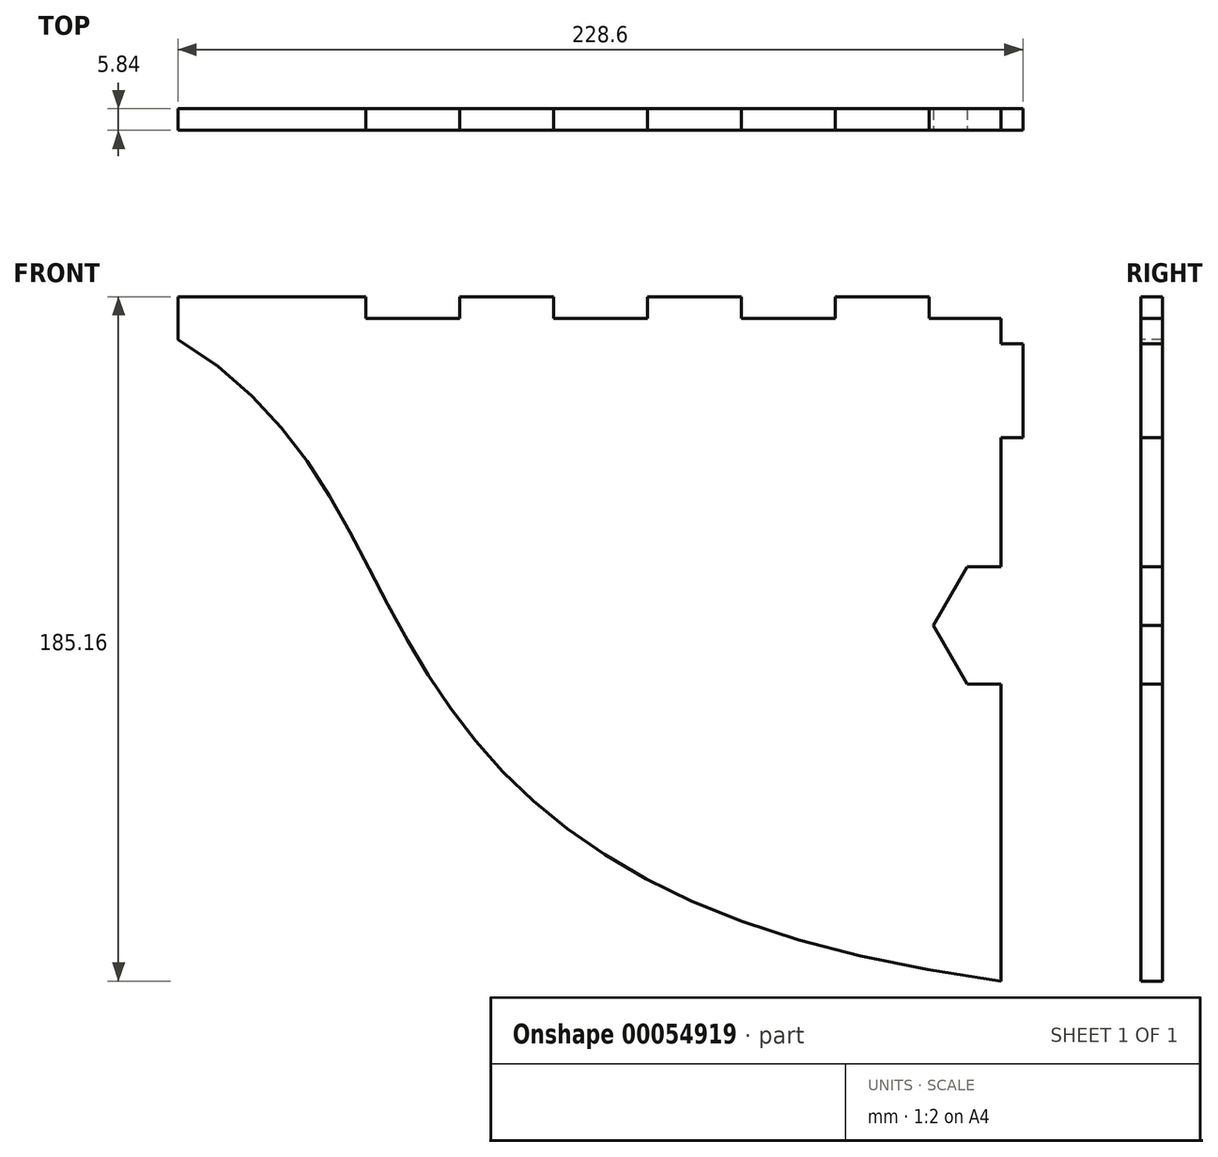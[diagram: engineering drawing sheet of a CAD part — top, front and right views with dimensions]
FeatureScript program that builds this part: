
annotation { "Feature Type Name" : "Feature", "Feature Type Description" : "" }
export const myFeature = defineFeature(function(context is Context, id is Id, definition is map)
    precondition{}
    {
        {
            var Q0;
            Q0=qCreatedBy(makeId("Front.planeOp"),FACE);
            var sketch = newSketch(context, id + "F0", { "sketchPlane" : qUnion([Q0])});
            skLineSegment(sketch, "E0.bottom", {"start": v(-113.95, 205.98) * mm, "end": v(165.45, 205.98) * mm});
            skLineSegment(sketch, "E0.top", {"start": v(-113.95, -124.22) * mm, "end": v(165.45, -124.22) * mm});
            skLineSegment(sketch, "E0.left", {"start": v(-113.95, 205.98) * mm, "end": v(-113.95, -124.22) * mm});
            skLineSegment(sketch, "E0.right", {"start": v(165.45, 205.98) * mm, "end": v(165.45, -124.22) * mm});
            skSolve(sketch);
        }
        {
            var Q0;
            Q0=makeQuery(id+"F0.imprint","IMPRINT",FACE,{"disambiguationData":[TD([[makeQuery(id+"F0.imprint","IMPRINT",EDGE,{"derivedFrom":sQuery(id+"F0.wireOp",EDGE,"E0.bottom")}),-1.0]])]});
            extrude(context, id + "F1", {"entities" : qUnion([Q0]), "depth" : 5.84 * mm});
        }
        {
            var Q0;
            Q0=makeQuery(id+"F1.opExtrude","CAP_FACE",FACE,{"disambiguationData":[OSD([sQuery(id+"F0.wireOp",EDGE,"E0.bottom"),sQuery(id+"F0.wireOp",EDGE,"E0.top"),sQuery(id+"F0.wireOp",EDGE,"E0.left"),sQuery(id+"F0.wireOp",EDGE,"E0.right")])],"isStart":false});
            var sketch = newSketch(context, id + "F2", { "sketchPlane" : qUnion([Q0])});
            skLineSegment(sketch, "E1", {"start": v(165.45, -118.38) * mm, "end": v(140.05, -118.38) * mm});
            skLineSegment(sketch, "E2", {"start": v(140.05, -118.38) * mm, "end": v(140.05, -124.22) * mm});
            skLineSegment(sketch, "E3", {"start": v(140.05, -124.22) * mm, "end": v(114.65, -124.22) * mm});
            skLineSegment(sketch, "E4", {"start": v(114.65, -124.22) * mm, "end": v(114.65, -118.38) * mm});
            skLineSegment(sketch, "E5", {"start": v(114.65, -118.38) * mm, "end": v(89.25, -118.38) * mm});
            skLineSegment(sketch, "E6", {"start": v(89.25, -118.38) * mm, "end": v(89.25, -124.22) * mm});
            skLineSegment(sketch, "E7", {"start": v(89.25, -124.22) * mm, "end": v(63.85, -124.22) * mm});
            skLineSegment(sketch, "E8", {"start": v(63.85, -124.22) * mm, "end": v(63.85, -118.38) * mm});
            skLineSegment(sketch, "E9", {"start": v(63.85, -118.38) * mm, "end": v(38.45, -118.38) * mm});
            skLineSegment(sketch, "E10", {"start": v(38.45, -118.38) * mm, "end": v(38.45, -124.22) * mm});
            skLineSegment(sketch, "E11", {"start": v(38.45, -124.22) * mm, "end": v(13.05, -124.22) * mm});
            skLineSegment(sketch, "E12", {"start": v(13.05, -124.22) * mm, "end": v(13.05, -118.38) * mm});
            skLineSegment(sketch, "E13", {"start": v(13.05, -118.38) * mm, "end": v(-12.35, -118.38) * mm});
            skLineSegment(sketch, "E14", {"start": v(-12.35, -118.38) * mm, "end": v(-12.35, -124.22) * mm});
            skLineSegment(sketch, "E15", {"start": v(-12.35, -124.22) * mm, "end": v(-37.75, -124.22) * mm});
            skLineSegment(sketch, "E16", {"start": v(-37.75, -124.22) * mm, "end": v(-37.75, -118.38) * mm});
            skLineSegment(sketch, "E17", {"start": v(-37.75, -118.38) * mm, "end": v(-113.95, -118.38) * mm});
            skLineSegment(sketch, "E18", {"start": v(-113.95, -118.38) * mm, "end": v(-113.95, -124.22) * mm});
            skLineSegment(sketch, "E19", {"start": v(-113.95, -124.22) * mm, "end": v(-37.75, -124.22) * mm});
            skLineSegment(sketch, "E20.bottom", {"start": v(165.45, -98.82) * mm, "end": v(159.6, -98.82) * mm});
            skLineSegment(sketch, "E20.top", {"start": v(165.45, -73.42) * mm, "end": v(159.6, -73.42) * mm});
            skLineSegment(sketch, "E20.left", {"start": v(165.45, -98.82) * mm, "end": v(165.45, -73.42) * mm});
            skLineSegment(sketch, "E20.right", {"start": v(159.6, -98.82) * mm, "end": v(159.6, -73.42) * mm});
            skLineSegment(sketch, "E21.bottom", {"start": v(165.45, -48.02) * mm, "end": v(159.6, -48.02) * mm});
            skLineSegment(sketch, "E21.top", {"start": v(165.45, -9.92) * mm, "end": v(159.6, -9.92) * mm});
            skLineSegment(sketch, "E21.left", {"start": v(165.45, -48.02) * mm, "end": v(165.45, -9.92) * mm});
            skLineSegment(sketch, "E21.right", {"start": v(159.6, -48.02) * mm, "end": v(159.6, -9.92) * mm});
            skLineSegment(sketch, "E22.bottom", {"start": v(-113.95, -98.82) * mm, "end": v(-108.1, -98.82) * mm});
            skLineSegment(sketch, "E22.top", {"start": v(-113.95, -73.42) * mm, "end": v(-108.1, -73.42) * mm});
            skLineSegment(sketch, "E22.left", {"start": v(-113.95, -98.82) * mm, "end": v(-113.95, -73.42) * mm});
            skLineSegment(sketch, "E22.right", {"start": v(-108.1, -98.82) * mm, "end": v(-108.1, -73.42) * mm});
            skLineSegment(sketch, "E23.bottom", {"start": v(-113.95, -48.02) * mm, "end": v(-108.1, -48.02) * mm});
            skLineSegment(sketch, "E23.top", {"start": v(-113.95, -22.62) * mm, "end": v(-108.1, -22.62) * mm});
            skLineSegment(sketch, "E23.left", {"start": v(-113.95, -48.02) * mm, "end": v(-113.95, -22.62) * mm});
            skLineSegment(sketch, "E23.right", {"start": v(-108.1, -48.02) * mm, "end": v(-108.1, -22.62) * mm});
            skLineSegment(sketch, "E24.bottom", {"start": v(-113.95, 2.78) * mm, "end": v(-108.1, 2.78) * mm});
            skLineSegment(sketch, "E24.top", {"start": v(-113.95, 28.18) * mm, "end": v(-108.1, 28.18) * mm});
            skLineSegment(sketch, "E24.left", {"start": v(-113.95, 2.78) * mm, "end": v(-113.95, 28.18) * mm});
            skLineSegment(sketch, "E24.right", {"start": v(-108.1, 2.78) * mm, "end": v(-108.1, 28.18) * mm});
            skLineSegment(sketch, "E25.bottom", {"start": v(-113.95, 104.38) * mm, "end": v(-108.1, 104.38) * mm});
            skLineSegment(sketch, "E25.top", {"start": v(-113.95, 129.78) * mm, "end": v(-108.1, 129.78) * mm});
            skLineSegment(sketch, "E25.left", {"start": v(-113.95, 104.38) * mm, "end": v(-113.95, 129.78) * mm});
            skLineSegment(sketch, "E25.right", {"start": v(-108.1, 104.38) * mm, "end": v(-108.1, 129.78) * mm});
            skLineSegment(sketch, "E26.bottom", {"start": v(-113.95, 53.58) * mm, "end": v(-108.1, 53.58) * mm});
            skLineSegment(sketch, "E26.top", {"start": v(-113.95, 78.98) * mm, "end": v(-108.1, 78.98) * mm});
            skLineSegment(sketch, "E26.left", {"start": v(-113.95, 53.58) * mm, "end": v(-113.95, 78.98) * mm});
            skLineSegment(sketch, "E26.right", {"start": v(-108.1, 53.58) * mm, "end": v(-108.1, 78.98) * mm});
            skLineSegment(sketch, "E27.bottom", {"start": v(-113.95, 155.18) * mm, "end": v(-108.1, 155.18) * mm});
            skLineSegment(sketch, "E27.top", {"start": v(-113.95, 180.58) * mm, "end": v(-108.1, 180.58) * mm});
            skLineSegment(sketch, "E27.left", {"start": v(-113.95, 155.18) * mm, "end": v(-113.95, 180.58) * mm});
            skLineSegment(sketch, "E27.right", {"start": v(-108.1, 155.18) * mm, "end": v(-108.1, 180.58) * mm});
            skSolve(sketch);
        }
        {
            var Q0;
            {var subQ0=sQuery(id+"F2.wireOp",EDGE,"E1");Q0=makeQuery(id+"F2.imprint","IMPRINT",FACE,{"disambiguationData":[TD([[makeQuery(id+"F2.imprint","IMPRINT",EDGE,{"derivedFrom":subQ0}),1.0]])]});}
            var Q1;
            {var subQ0=sQuery(id+"F2.wireOp",EDGE,"E4");Q1=makeQuery(id+"F2.imprint","IMPRINT",FACE,{"disambiguationData":[TD([[makeQuery(id+"F2.imprint","IMPRINT",EDGE,{"derivedFrom":subQ0}),1.0]])]});}
            var Q2;
            {var subQ0=sQuery(id+"F2.wireOp",EDGE,"E8");Q2=makeQuery(id+"F2.imprint","IMPRINT",FACE,{"disambiguationData":[TD([[makeQuery(id+"F2.imprint","IMPRINT",EDGE,{"derivedFrom":subQ0}),1.0]])]});}
            var Q3;
            {var subQ0=sQuery(id+"F2.wireOp",EDGE,"E12");Q3=makeQuery(id+"F2.imprint","IMPRINT",FACE,{"disambiguationData":[TD([[makeQuery(id+"F2.imprint","IMPRINT",EDGE,{"derivedFrom":subQ0}),1.0]])]});}
            var Q4;
            Q4=makeQuery(id+"F2.imprint","IMPRINT",FACE,{"disambiguationData":[TD([[makeQuery(id+"F2.imprint","IMPRINT",EDGE,{"derivedFrom":sQuery(id+"F2.wireOp",EDGE,"E16")}),1.0]])]});
            var Q5;
            Q5=makeQuery(id+"F2.imprint","IMPRINT",FACE,{"disambiguationData":[TD([[makeQuery(id+"F2.imprint","IMPRINT",EDGE,{"derivedFrom":sQuery(id+"F2.wireOp",EDGE,"E20.bottom")}),-1.0]])]});
            var Q6;
            Q6=makeQuery(id+"F2.imprint","IMPRINT",FACE,{"disambiguationData":[TD([[makeQuery(id+"F2.imprint","IMPRINT",EDGE,{"derivedFrom":sQuery(id+"F2.wireOp",EDGE,"E21.bottom")}),-1.0]])]});
            var Q7;
            Q7=makeQuery(id+"F2.imprint","IMPRINT",FACE,{"disambiguationData":[TD([[makeQuery(id+"F2.imprint","IMPRINT",EDGE,{"derivedFrom":sQuery(id+"F2.wireOp",EDGE,"E22.bottom")}),1.0]])]});
            var Q8;
            Q8=makeQuery(id+"F2.imprint","IMPRINT",FACE,{"disambiguationData":[TD([[makeQuery(id+"F2.imprint","IMPRINT",EDGE,{"derivedFrom":sQuery(id+"F2.wireOp",EDGE,"E23.bottom")}),1.0]])]});
            var Q9;
            Q9=makeQuery(id+"F2.imprint","IMPRINT",FACE,{"disambiguationData":[TD([[makeQuery(id+"F2.imprint","IMPRINT",EDGE,{"derivedFrom":sQuery(id+"F2.wireOp",EDGE,"E24.bottom")}),1.0]])]});
            var Q10;
            Q10=makeQuery(id+"F2.imprint","IMPRINT",FACE,{"disambiguationData":[TD([[makeQuery(id+"F2.imprint","IMPRINT",EDGE,{"derivedFrom":sQuery(id+"F2.wireOp",EDGE,"E26.bottom")}),1.0]])]});
            var Q11;
            Q11=makeQuery(id+"F2.imprint","IMPRINT",FACE,{"disambiguationData":[TD([[makeQuery(id+"F2.imprint","IMPRINT",EDGE,{"derivedFrom":sQuery(id+"F2.wireOp",EDGE,"E27.bottom")}),1.0]])]});
            var Q12;
            Q12=makeQuery(id+"F2.imprint","IMPRINT",FACE,{"disambiguationData":[TD([[makeQuery(id+"F2.imprint","IMPRINT",EDGE,{"derivedFrom":sQuery(id+"F2.wireOp",EDGE,"E25.bottom")}),1.0]])]});
            var Q13;
            Q13=makeQuery(id+"F1.opExtrude","CAP_FACE",FACE,{"disambiguationData":[OSD([sQuery(id+"F0.wireOp",EDGE,"E0.bottom"),sQuery(id+"F0.wireOp",EDGE,"E0.top"),sQuery(id+"F0.wireOp",EDGE,"E0.left"),sQuery(id+"F0.wireOp",EDGE,"E0.right")])],"isStart":true});
            extrude(context, id + "F3", {"entities" : qUnion([Q0, Q1, Q2, Q3, Q4, Q5, Q6, Q7, Q8, Q9, Q10, Q11, Q12]), "operationType" : NewBodyOperationType.REMOVE, "endBound" : BoundingType.UP_TO_SURFACE, "oppositeDirection" : true, "endBoundEntityFace" : qUnion([Q13]), "depth" : 25.4 * mm});
        }
        {
            var Q0;
            Q0=makeQuery(id+"F1.opExtrude","CAP_FACE",FACE,{"disambiguationData":[OSD([sQuery(id+"F0.wireOp",EDGE,"E0.bottom"),sQuery(id+"F0.wireOp",EDGE,"E0.top"),sQuery(id+"F0.wireOp",EDGE,"E0.left"),sQuery(id+"F0.wireOp",EDGE,"E0.right")])],"isStart":false});
            var sketch = newSketch(context, id + "F4", { "sketchPlane" : qUnion([Q0])});
            skPoint(sketch, "E28", {"position": v(-56.8, 205.98) * mm});
            skPoint(sketch, "E29", {"position": v(0.35, 205.98) * mm});
            skPoint(sketch, "E30", {"position": v(57.5, 205.98) * mm});
            skPoint(sketch, "E31", {"position": v(159.6, 15.48) * mm});
            skFitSpline(sketch, "E32", {"points": [v(159.6, 15.48) * mm, v(0, 86.75) * mm, v(-113.95, 205.98) * mm], "startDerivative": vector(-509.98, 75.1) * mm, "endDerivative": vector(-560.6, 77.32) * mm});
            skLineSegment(sketch, "E33", {"start": v(159.6, 15.48) * mm, "end": v(165.45, 15.48) * mm});
            skFitSpline(sketch, "E34", {"points": [v(159.6, 21.83) * mm, v(0, 112.15) * mm, v(-113.95, 212.33) * mm], "startDerivative": vector(-548.57, 72.75) * mm, "endDerivative": vector(-499.93, 79.99) * mm});
            skLineSegment(sketch, "E35", {"start": v(-113.95, 212.33) * mm, "end": v(-113.95, 205.98) * mm});
            skLineSegment(sketch, "E36", {"start": v(159.6, 21.83) * mm, "end": v(159.6, 15.48) * mm});
            skSolve(sketch);
        }
        {
            var Q0;
            Q0=makeQuery(id+"F1.opExtrude","CAP_FACE",FACE,{"disambiguationData":[OSD([sQuery(id+"F0.wireOp",EDGE,"E0.bottom"),sQuery(id+"F0.wireOp",EDGE,"E0.top"),sQuery(id+"F0.wireOp",EDGE,"E0.left"),sQuery(id+"F0.wireOp",EDGE,"E0.right")])],"isStart":false});
            var sketch = newSketch(context, id + "F5", { "sketchPlane" : qUnion([Q0])});
            skLineSegment(sketch, "E37.bottom", {"start": v(165.45, -3.57) * mm, "end": v(159.6, -3.57) * mm});
            skLineSegment(sketch, "E37.top", {"start": v(165.45, 9.13) * mm, "end": v(159.6, 9.13) * mm});
            skLineSegment(sketch, "E37.left", {"start": v(165.45, -3.57) * mm, "end": v(165.45, 9.13) * mm});
            skLineSegment(sketch, "E37.right", {"start": v(159.6, -3.57) * mm, "end": v(159.6, 9.13) * mm});
            skSolve(sketch);
        }
        {
            var Q0;
            Q0=makeQuery(id+"F5.imprint","IMPRINT",FACE,{"disambiguationData":[TD([[makeQuery(id+"F5.imprint","IMPRINT",EDGE,{"derivedFrom":sQuery(id+"F5.wireOp",EDGE,"E37.bottom")}),-1.0]])]});
            var Q1;
            Q1=makeQuery(id+"F1.opExtrude","CAP_FACE",FACE,{"disambiguationData":[OSD([sQuery(id+"F0.wireOp",EDGE,"E0.bottom"),sQuery(id+"F0.wireOp",EDGE,"E0.top"),sQuery(id+"F0.wireOp",EDGE,"E0.left"),sQuery(id+"F0.wireOp",EDGE,"E0.right")])],"isStart":true});
            extrude(context, id + "F6", {"entities" : qUnion([Q0]), "operationType" : NewBodyOperationType.REMOVE, "endBound" : BoundingType.UP_TO_SURFACE, "oppositeDirection" : true, "endBoundEntityFace" : qUnion([Q1]), "depth" : 25.4 * mm});
        }
        {
            var Q0;
            Q0=makeQuery(id+"F4.imprint","IMPRINT",FACE,{"disambiguationData":[TD([[makeQuery(id+"F4.imprint","IMPRINT",EDGE,{"derivedFrom":sQuery(id+"F4.wireOp",EDGE,"E32")}),1.0]])]});
            var Q1;
            {var subQ0=sQuery(id+"F4.wireOp",EDGE,"E32");Q1=makeQuery(id+"F4.imprint","IMPRINT",FACE,{"disambiguationData":[TD([[makeQuery(id+"F4.imprint","IMPRINT",EDGE,{"derivedFrom":subQ0}),-1.0]])]});}
            var Q2;
            Q2=makeQuery(id+"F1.opExtrude","CAP_FACE",FACE,{"disambiguationData":[OSD([sQuery(id+"F0.wireOp",EDGE,"E0.bottom"),sQuery(id+"F0.wireOp",EDGE,"E0.top"),sQuery(id+"F0.wireOp",EDGE,"E0.left"),sQuery(id+"F0.wireOp",EDGE,"E0.right")])],"isStart":true});
            extrude(context, id + "F7", {"entities" : qUnion([Q0, Q1]), "operationType" : NewBodyOperationType.REMOVE, "endBound" : BoundingType.UP_TO_SURFACE, "oppositeDirection" : true, "endBoundEntityFace" : qUnion([Q2]), "depth" : 25.4 * mm});
        }
        {
            var Q0;
            Q0=makeQuery(id+"F1.opExtrude","CAP_FACE",FACE,{"disambiguationData":[OSD([sQuery(id+"F0.wireOp",EDGE,"E0.bottom"),sQuery(id+"F0.wireOp",EDGE,"E0.top"),sQuery(id+"F0.wireOp",EDGE,"E0.left"),sQuery(id+"F0.wireOp",EDGE,"E0.right")])],"isStart":false});
            var sketch = newSketch(context, id + "F8", { "sketchPlane" : qUnion([Q0])});
            skLineSegment(sketch, "E38.bottom", {"start": v(165.45, 28.18) * mm, "end": v(159.6, 28.18) * mm});
            skLineSegment(sketch, "E38.top", {"start": v(165.45, 53.58) * mm, "end": v(159.6, 53.58) * mm});
            skLineSegment(sketch, "E38.left", {"start": v(165.45, 28.18) * mm, "end": v(165.45, 53.58) * mm});
            skLineSegment(sketch, "E38.right", {"start": v(159.6, 28.18) * mm, "end": v(159.6, 53.58) * mm});
            skLineSegment(sketch, "E39.bottom", {"start": v(165.45, 168.9) * mm, "end": v(159.6, 168.9) * mm});
            skLineSegment(sketch, "E39.top", {"start": v(165.45, 194.3) * mm, "end": v(159.6, 194.3) * mm});
            skLineSegment(sketch, "E39.left", {"start": v(165.45, 168.9) * mm, "end": v(165.45, 194.3) * mm});
            skLineSegment(sketch, "E39.right", {"start": v(159.6, 168.9) * mm, "end": v(159.6, 194.3) * mm});
            skLineSegment(sketch, "E40", {"start": v(159.6, 194.3) * mm, "end": v(159.6, 205.98) * mm});
            skLineSegment(sketch, "E41", {"start": v(159.6, 168.9) * mm, "end": v(159.6, 53.58) * mm});
            skLineSegment(sketch, "E42", {"start": v(159.6, 28.18) * mm, "end": v(159.6, 21.83) * mm});
            skCircle(sketch, "E43", {"center": v(159.6, 118.1) * mm, "radius": 15.88 * mm});
            skCircle(sketch, "E44.cCircle", {"center": v(159.6, 118.1) * mm, "radius": 15.87 * mm, "construction": true});
            skLineSegment(sketch, "E44.0", {"start": v(150.44, 133.97) * mm, "end": v(168.77, 133.97) * mm});
            skLineSegment(sketch, "E44.1", {"start": v(168.77, 133.97) * mm, "end": v(177.94, 118.1) * mm});
            skLineSegment(sketch, "E44.2", {"start": v(177.94, 118.1) * mm, "end": v(168.77, 102.22) * mm});
            skLineSegment(sketch, "E44.3", {"start": v(168.77, 102.22) * mm, "end": v(150.44, 102.22) * mm});
            skLineSegment(sketch, "E44.4", {"start": v(150.44, 102.22) * mm, "end": v(141.28, 118.1) * mm});
            skLineSegment(sketch, "E44.5", {"start": v(141.28, 118.1) * mm, "end": v(150.44, 133.97) * mm});
            skPoint(sketch, "E44.0.midPoint", {"position": v(159.6, 133.97) * mm});
            skSolve(sketch);
        }
        {
            var Q0;
            {var subQ7=sQuery(id+"F8.wireOp",EDGE,"E38.bottom");Q0=makeQuery(id+"F8.imprint","IMPRINT",FACE,{"disambiguationData":[TD([[makeQuery(id+"F8.imprint","IMPRINT",EDGE,{"derivedFrom":subQ7}),1.0]])]});}
            var Q1;
            {var subQ0=sQuery(id+"F8.wireOp",EDGE,"E38.top");Q1=makeQuery(id+"F8.imprint","IMPRINT",FACE,{"disambiguationData":[TD([[makeQuery(id+"F8.imprint","IMPRINT",EDGE,{"derivedFrom":subQ0}),-1.0]])]});}
            var Q2;
            {var subQ0=sQuery(id+"F8.wireOp",EDGE,"E39.top");Q2=makeQuery(id+"F8.imprint","IMPRINT",FACE,{"disambiguationData":[TD([[makeQuery(id+"F8.imprint","IMPRINT",EDGE,{"derivedFrom":subQ0}),-1.0]])]});}
            var Q3;
            Q3=makeQuery(id+"F8.imprint","IMPRINT",FACE,{"disambiguationData":[TD([[makeQuery(id+"F8.imprint","IMPRINT",EDGE,{"derivedFrom":sQuery(id+"F8.wireOp",EDGE,"E38.bottom")}),-1.0]])]});
            var Q4;
            {var subQ0=sQuery(id+"F8.wireOp",EDGE,"E39.bottom");Q4=makeQuery(id+"F8.imprint","IMPRINT",FACE,{"disambiguationData":[TD([[makeQuery(id+"F8.imprint","IMPRINT",EDGE,{"derivedFrom":subQ0}),1.0]])]});}
            var Q5;
            {var subQ0=sQuery(id+"F8.wireOp",EDGE,"E43");var subQ1=sQuery(id+"F8.wireOp",EDGE,"E41");var subQ2=makeQuery(id+"F8.imprint","INTERSECT",VERTEX,{"disambiguationData":[OD(0.0)],"derivedFrom":[subQ1,subQ0]});Q5=makeQuery(id+"F8.imprint","IMPRINT",FACE,{"disambiguationData":[TD([[makeQuery(id+"F8.imprint","IMPRINT",EDGE,{"disambiguationData":[TD([[subQ2,-1.0]])],"derivedFrom":subQ1}),1.0]])]});}
            var Q6;
            {var subQ0=sQuery(id+"F8.wireOp",EDGE,"E43");var subQ1=sQuery(id+"F8.wireOp",EDGE,"E41");var subQ2=makeQuery(id+"F8.imprint","INTERSECT",VERTEX,{"disambiguationData":[OD(0.0)],"derivedFrom":[subQ1,subQ0]});Q6=makeQuery(id+"F8.imprint","IMPRINT",FACE,{"disambiguationData":[TD([[makeQuery(id+"F8.imprint","IMPRINT",EDGE,{"disambiguationData":[TD([[subQ2,-1.0]])],"derivedFrom":subQ1}),-1.0]])]});}
            var Q7;
            Q7=makeQuery(id+"F8.imprint","IMPRINT",FACE,{"disambiguationData":[TD([[makeQuery(id+"F8.imprint","IMPRINT",EDGE,{"derivedFrom":sQuery(id+"F8.wireOp",EDGE,"911f7886-06e0-41c8-baab-f06c2c8cfe31.bottom")}),-1.0]])]});
            var Q8;
            Q8=makeQuery(id+"F8.imprint","IMPRINT",FACE,{"disambiguationData":[TD([[makeQuery(id+"F8.imprint","IMPRINT",EDGE,{"derivedFrom":sQuery(id+"F8.wireOp",EDGE,"12f187d2-8b28-4778-8ae5-448a27c9e400.bottom")}),-1.0]])]});
            var Q9;
            {var subQ5=sQuery(id+"F8.wireOp",EDGE,"6e0f9fa3-966a-40a3-b50c-f366dbc922a8.left");Q9=makeQuery(id+"F8.imprint","IMPRINT",FACE,{"disambiguationData":[TD([[makeQuery(id+"F8.imprint","IMPRINT",EDGE,{"derivedFrom":subQ5}),1.0]])]});}
            var Q10;
            {var subQ5=sQuery(id+"F8.wireOp",EDGE,"6e0f9fa3-966a-40a3-b50c-f366dbc922a8.right");Q10=makeQuery(id+"F8.imprint","IMPRINT",FACE,{"disambiguationData":[TD([[makeQuery(id+"F8.imprint","IMPRINT",EDGE,{"derivedFrom":subQ5}),-1.0]])]});}
            var Q11;
            {var subQ0=sQuery(id+"F8.wireOp",EDGE,"E44.5");var subQ3=sQuery(id+"F8.wireOp",EDGE,"E44.0");var subQ5=makeQuery(id+"F8.imprint","INTERSECT",VERTEX,{"derivedFrom":[subQ3,subQ0]});Q11=makeQuery(id+"F8.imprint","IMPRINT",FACE,{"disambiguationData":[TD([[makeQuery(id+"F8.imprint","IMPRINT",EDGE,{"disambiguationData":[TD([[subQ5,1.0]])],"derivedFrom":subQ0}),-1.0]])]});}
            var Q12;
            {var subQ0=sQuery(id+"F8.wireOp",EDGE,"E44.5");var subQ1=sQuery(id+"F8.wireOp",EDGE,"E43");var subQ2=makeQuery(id+"F8.imprint","INTERSECT",VERTEX,{"derivedFrom":[subQ1,subQ0]});Q12=makeQuery(id+"F8.imprint","IMPRINT",FACE,{"disambiguationData":[TD([[makeQuery(id+"F8.imprint","IMPRINT",EDGE,{"disambiguationData":[TD([[subQ2,-1.0]])],"derivedFrom":subQ1}),-1.0]])]});}
            var Q13;
            {var subQ0=sQuery(id+"F8.wireOp",EDGE,"E44.4");var subQ3=sQuery(id+"F8.wireOp",EDGE,"E44.3");var subQ5=makeQuery(id+"F8.imprint","INTERSECT",VERTEX,{"derivedFrom":[subQ3,subQ0]});Q13=makeQuery(id+"F8.imprint","IMPRINT",FACE,{"disambiguationData":[TD([[makeQuery(id+"F8.imprint","IMPRINT",EDGE,{"disambiguationData":[TD([[subQ5,-1.0]])],"derivedFrom":subQ0}),-1.0]])]});}
            var Q14;
            {var subQ0=sQuery(id+"F8.wireOp",EDGE,"E44.0");var subQ1=sQuery(id+"F8.wireOp",EDGE,"E43");var subQ2=makeQuery(id+"F8.imprint","INTERSECT",VERTEX,{"derivedFrom":[sQuery(id+"F8.wireOp",EDGE,"E41"),subQ1,subQ0]});Q14=makeQuery(id+"F8.imprint","IMPRINT",FACE,{"disambiguationData":[TD([[makeQuery(id+"F8.imprint","IMPRINT",EDGE,{"disambiguationData":[TD([[subQ2,1.0]])],"derivedFrom":subQ1}),-1.0]])]});}
            var Q15;
            {var subQ0=sQuery(id+"F8.wireOp",EDGE,"E44.3");var subQ1=sQuery(id+"F8.wireOp",EDGE,"E43");var subQ2=makeQuery(id+"F8.imprint","INTERSECT",VERTEX,{"derivedFrom":[sQuery(id+"F8.wireOp",EDGE,"E41"),subQ1,subQ0]});Q15=makeQuery(id+"F8.imprint","IMPRINT",FACE,{"disambiguationData":[TD([[makeQuery(id+"F8.imprint","IMPRINT",EDGE,{"disambiguationData":[TD([[subQ2,-1.0]])],"derivedFrom":subQ1}),-1.0]])]});}
            var Q16;
            Q16=makeQuery(id+"F1.opExtrude","CAP_FACE",FACE,{"disambiguationData":[OSD([sQuery(id+"F0.wireOp",EDGE,"E0.bottom"),sQuery(id+"F0.wireOp",EDGE,"E0.top"),sQuery(id+"F0.wireOp",EDGE,"E0.left"),sQuery(id+"F0.wireOp",EDGE,"E0.right")])],"isStart":true});
            extrude(context, id + "F9", {"entities" : qUnion([Q0, Q1, Q2, Q3, Q4, Q5, Q6, Q7, Q8, Q9, Q10, Q11, Q12, Q13, Q14, Q15]), "operationType" : NewBodyOperationType.REMOVE, "endBound" : BoundingType.UP_TO_SURFACE, "oppositeDirection" : true, "endBoundEntityFace" : qUnion([Q16]), "depth" : 25.4 * mm});
        }
        {
            var Q0;
            Q0=makeQuery(id+"F1.opExtrude","CAP_FACE",FACE,{"disambiguationData":[OSD([sQuery(id+"F0.wireOp",EDGE,"E0.bottom"),sQuery(id+"F0.wireOp",EDGE,"E0.top"),sQuery(id+"F0.wireOp",EDGE,"E0.left"),sQuery(id+"F0.wireOp",EDGE,"E0.right")])],"isStart":false});
            var sketch = newSketch(context, id + "F10", { "sketchPlane" : qUnion([Q0])});
            skLineSegment(sketch, "E45.bottom", {"start": v(159.6, 205.98) * mm, "end": v(-87.11, 205.98) * mm});
            skLineSegment(sketch, "E45.top", {"start": v(159.6, 207) * mm, "end": v(-87.11, 207) * mm});
            skLineSegment(sketch, "E45.left", {"start": v(159.6, 205.98) * mm, "end": v(159.6, 207) * mm});
            skLineSegment(sketch, "E45.right", {"start": v(-87.11, 205.98) * mm, "end": v(-87.11, 207) * mm});
            skSolve(sketch);
        }
        {
            var Q0;
            Q0=makeQuery(id+"F10.imprint","IMPRINT",FACE,{"disambiguationData":[TD([[makeQuery(id+"F10.imprint","IMPRINT",EDGE,{"derivedFrom":sQuery(id+"F10.wireOp",EDGE,"E45.bottom")}),1.0]])]});
            var Q1;
            Q1=makeQuery(id+"F1.opExtrude","CAP_FACE",FACE,{"disambiguationData":[OSD([sQuery(id+"F0.wireOp",EDGE,"E0.bottom"),sQuery(id+"F0.wireOp",EDGE,"E0.top"),sQuery(id+"F0.wireOp",EDGE,"E0.left"),sQuery(id+"F0.wireOp",EDGE,"E0.right")])],"isStart":true});
            extrude(context, id + "F11", {"entities" : qUnion([Q0]), "operationType" : NewBodyOperationType.ADD, "endBound" : BoundingType.UP_TO_SURFACE, "oppositeDirection" : true, "endBoundEntityFace" : qUnion([Q1]), "depth" : 25.4 * mm});
        }
        {
            var Q0;
            Q0=makeQuery(id+"F11.boolean.opBoolean","MERGE",FACE,{"derivedFrom":[makeQuery(id+"F1.opExtrude","CAP_FACE",FACE,{"disambiguationData":[OSD([sQuery(id+"F0.wireOp",EDGE,"E0.bottom"),sQuery(id+"F0.wireOp",EDGE,"E0.top"),sQuery(id+"F0.wireOp",EDGE,"E0.left"),sQuery(id+"F0.wireOp",EDGE,"E0.right")])],"isStart":false}),makeQuery(id+"F11.opExtrude","CAP_FACE",FACE,{"disambiguationData":[OSD([sQuery(id+"F10.wireOp",EDGE,"E45.bottom"),sQuery(id+"F10.wireOp",EDGE,"E45.top"),sQuery(id+"F10.wireOp",EDGE,"E45.left"),sQuery(id+"F10.wireOp",EDGE,"E45.right")])],"isStart":true})]});
            var sketch = newSketch(context, id + "F12", { "sketchPlane" : qUnion([Q0])});
            skCircle(sketch, "E46", {"center": v(-36.31, 197.47) * mm, "radius": 3.18 * mm});
            skSolve(sketch);
        }
        {
            var Q0;
            Q0=makeQuery(id+"F12.imprint","IMPRINT",FACE,{"disambiguationData":[TD([[makeQuery(id+"F12.imprint","IMPRINT",EDGE,{"derivedFrom":sQuery(id+"F12.wireOp",EDGE,"E46")}),-1.0]])]});
            var sketch = newSketch(context, id + "F13", { "sketchPlane" : qUnion([Q0])});
            skLineSegment(sketch, "E47.bottom", {"start": v(159.6, 201.15) * mm, "end": v(140.05, 201.15) * mm});
            skLineSegment(sketch, "E47.top", {"start": v(159.6, 207) * mm, "end": v(140.05, 207) * mm});
            skLineSegment(sketch, "E47.left", {"start": v(159.6, 201.15) * mm, "end": v(159.6, 207) * mm});
            skLineSegment(sketch, "E47.right", {"start": v(140.05, 201.15) * mm, "end": v(140.05, 207) * mm});
            skLineSegment(sketch, "E48.bottom", {"start": v(114.65, 207) * mm, "end": v(89.25, 207) * mm});
            skLineSegment(sketch, "E48.top", {"start": v(114.65, 201.15) * mm, "end": v(89.25, 201.15) * mm});
            skLineSegment(sketch, "E48.left", {"start": v(89.25, 207) * mm, "end": v(89.25, 201.15) * mm});
            skLineSegment(sketch, "E48.right", {"start": v(114.65, 207) * mm, "end": v(114.65, 201.15) * mm});
            skLineSegment(sketch, "E49.bottom", {"start": v(63.85, 201.15) * mm, "end": v(38.45, 201.15) * mm});
            skLineSegment(sketch, "E49.top", {"start": v(63.85, 207) * mm, "end": v(38.45, 207) * mm});
            skLineSegment(sketch, "E49.left", {"start": v(63.85, 201.15) * mm, "end": v(63.85, 207) * mm});
            skLineSegment(sketch, "E49.right", {"start": v(38.45, 201.15) * mm, "end": v(38.45, 207) * mm});
            skPoint(sketch, "E50", {"position": v(-36.31, 172.98) * mm});
            skFitSpline(sketch, "E51", {"points": [v(-36.31, 172.98) * mm, v(-61.71, 192.03) * mm, v(-64.89, 207) * mm], "startDerivative": vector(-51.63, 38.72) * mm, "endDerivative": vector(-4.65, 81.64) * mm});
            skLineSegment(sketch, "E52.bottom", {"start": v(13.05, 207) * mm, "end": v(-12.35, 207) * mm});
            skLineSegment(sketch, "E52.top", {"start": v(13.05, 201.15) * mm, "end": v(-12.35, 201.15) * mm});
            skLineSegment(sketch, "E52.left", {"start": v(13.05, 207) * mm, "end": v(13.05, 201.15) * mm});
            skLineSegment(sketch, "E52.right", {"start": v(-12.35, 207) * mm, "end": v(-12.35, 201.15) * mm});
            skLineSegment(sketch, "E53", {"start": v(-63.15, 207) * mm, "end": v(-63.15, 193.64) * mm});
            skSolve(sketch);
        }
        {
            var Q0;
            Q0=makeQuery(id+"F13.imprint","IMPRINT",FACE,{"disambiguationData":[TD([[makeQuery(id+"F13.imprint","IMPRINT",EDGE,{"derivedFrom":sQuery(id+"F13.wireOp",EDGE,"E49.bottom")}),-1.0]])]});
            var Q1;
            Q1=makeQuery(id+"F13.imprint","IMPRINT",FACE,{"disambiguationData":[TD([[makeQuery(id+"F13.imprint","IMPRINT",EDGE,{"derivedFrom":sQuery(id+"F13.wireOp",EDGE,"E48.bottom")}),1.0]])]});
            var Q2;
            Q2=makeQuery(id+"F13.imprint","IMPRINT",FACE,{"disambiguationData":[TD([[makeQuery(id+"F13.imprint","IMPRINT",EDGE,{"derivedFrom":sQuery(id+"F13.wireOp",EDGE,"E47.bottom")}),-1.0]])]});
            var Q3;
            {var subQ5=makeQuery(id+"F12.imprint","IMPRINT",EDGE,{"derivedFrom":makeQuery(id+"F11.opExtrude","CAP_EDGE",EDGE,{"disambiguationData":[OSD([sQuery(id+"F10.wireOp",EDGE,"E45.right")])],"isStart":true})});Q3=makeQuery(id+"F13.imprint","IMPRINT",FACE,{"disambiguationData":[TD([[makeQuery(id+"F13.imprint","IMPRINT",EDGE,{"derivedFrom":subQ5}),-1.0]])]});}
            var Q4;
            Q4=makeQuery(id+"F13.imprint","IMPRINT",FACE,{"disambiguationData":[TD([[makeQuery(id+"F13.imprint","IMPRINT",EDGE,{"derivedFrom":sQuery(id+"F13.wireOp",EDGE,"E52.bottom")}),1.0]])]});
            var Q5;
            {var subQ0=sQuery(id+"F13.wireOp",EDGE,"E51");var subQ1=makeQuery(id+"F12.imprint","IMPRINT",EDGE,{"derivedFrom":makeQuery(id+"F11.opExtrude","CAP_EDGE",EDGE,{"disambiguationData":[OSD([sQuery(id+"F10.wireOp",EDGE,"E45.top")])],"isStart":true})});var subQ2=makeQuery(id+"F13.imprint","INTERSECT",VERTEX,{"derivedFrom":[subQ1,subQ0]});Q5=makeQuery(id+"F13.imprint","IMPRINT",FACE,{"disambiguationData":[TD([[makeQuery(id+"F13.imprint","IMPRINT",EDGE,{"disambiguationData":[TD([[subQ2,1.0]])],"derivedFrom":subQ0}),-1.0]])]});}
            var Q6;
            Q6=makeQuery(id+"F11.boolean.opBoolean","MERGE",FACE,{"derivedFrom":[makeQuery(id+"F1.opExtrude","CAP_FACE",FACE,{"disambiguationData":[OSD([sQuery(id+"F0.wireOp",EDGE,"E0.bottom"),sQuery(id+"F0.wireOp",EDGE,"E0.top"),sQuery(id+"F0.wireOp",EDGE,"E0.left"),sQuery(id+"F0.wireOp",EDGE,"E0.right")])],"isStart":true}),makeQuery(id+"F11.opExtrude","CAP_FACE",FACE,{"disambiguationData":[OSD([sQuery(id+"F10.wireOp",EDGE,"E45.bottom"),sQuery(id+"F10.wireOp",EDGE,"E45.top"),sQuery(id+"F10.wireOp",EDGE,"E45.left"),sQuery(id+"F10.wireOp",EDGE,"E45.right")])],"isStart":false})]});
            extrude(context, id + "F14", {"entities" : qUnion([Q0, Q1, Q2, Q3, Q4, Q5]), "operationType" : NewBodyOperationType.REMOVE, "endBound" : BoundingType.UP_TO_SURFACE, "oppositeDirection" : true, "endBoundEntityFace" : qUnion([Q6]), "depth" : 25.4 * mm});
        }
    });
